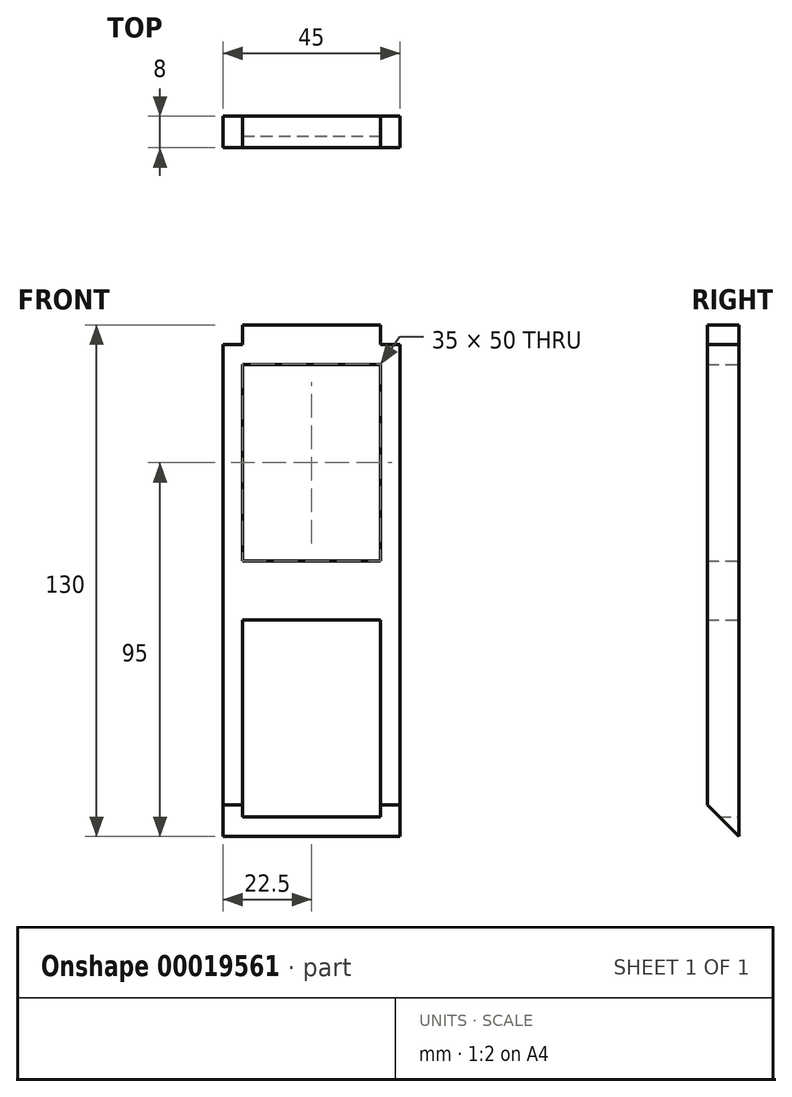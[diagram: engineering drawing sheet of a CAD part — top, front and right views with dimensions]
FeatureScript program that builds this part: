
annotation { "Feature Type Name" : "Feature", "Feature Type Description" : "" }
export const myFeature = defineFeature(function(context is Context, id is Id, definition is map)
    precondition{}
    {
        {
            var Q0;
            Q0=qCreatedBy(makeId("Front.planeOp"),FACE);
            var sketch = newSketch(context, id + "F0", { "sketchPlane" : qUnion([Q0])});
            skLineSegment(sketch, "E0.bottom", {"start": v(0, 0) * mm, "end": v(45, 0) * mm});
            skLineSegment(sketch, "E0.top", {"start": v(0, 125) * mm, "end": v(45, 125) * mm});
            skLineSegment(sketch, "E0.left", {"start": v(0, 0) * mm, "end": v(0, 125) * mm});
            skLineSegment(sketch, "E0.right", {"start": v(45, 0) * mm, "end": v(45, 125) * mm});
            skLineSegment(sketch, "E1.bottom", {"start": v(5, 120) * mm, "end": v(40, 120) * mm});
            skLineSegment(sketch, "E1.top", {"start": v(5, 70) * mm, "end": v(40, 70) * mm});
            skLineSegment(sketch, "E1.left", {"start": v(5, 120) * mm, "end": v(5, 70) * mm});
            skLineSegment(sketch, "E1.right", {"start": v(40, 120) * mm, "end": v(40, 70) * mm});
            skLineSegment(sketch, "E2.bottom", {"start": v(5, 55) * mm, "end": v(40, 55) * mm});
            skLineSegment(sketch, "E2.top", {"start": v(5, 5) * mm, "end": v(40, 5) * mm});
            skLineSegment(sketch, "E2.left", {"start": v(5, 55) * mm, "end": v(5, 5) * mm});
            skLineSegment(sketch, "E2.right", {"start": v(40, 55) * mm, "end": v(40, 5) * mm});
            skSolve(sketch);
        }
        {
            var Q0;
            Q0=makeQuery(id+"F0.imprint","IMPRINT",FACE,{"disambiguationData":[TD([[makeQuery(id+"F0.imprint","IMPRINT",EDGE,{"derivedFrom":sQuery(id+"F0.wireOp",EDGE,"E0.bottom")}),1.0]])]});
            extrude(context, id + "F1", {"entities" : qUnion([Q0]), "depth" : 8 * mm, "offsetDistance" : 25 * mm});
        }
        {
            var Q0;
            Q0=makeQuery(id+"F1.opExtrude","SWEPT_FACE",FACE,{"disambiguationData":[OSD([sQuery(id+"F0.wireOp",EDGE,"E0.top")])]});
            var sketch = newSketch(context, id + "F2", { "sketchPlane" : qUnion([Q0])});
            skLineSegment(sketch, "E3.bottom", {"start": v(5, 0) * mm, "end": v(40, 0) * mm});
            skLineSegment(sketch, "E3.top", {"start": v(5, -8) * mm, "end": v(40, -8) * mm});
            skLineSegment(sketch, "E3.left", {"start": v(5, 0) * mm, "end": v(5, -8) * mm});
            skLineSegment(sketch, "E3.right", {"start": v(40, 0) * mm, "end": v(40, -8) * mm});
            skSolve(sketch);
        }
        {
            var Q0;
            Q0 = qSketchRegion(id + "F2", true);
            extrude(context, id + "F3", {"entities" : qUnion([Q0]), "operationType" : NewBodyOperationType.ADD, "depth" : 5 * mm, "offsetDistance" : 25 * mm});
        }
        {
            var Q0;
            Q0=makeQuery(id+"F1.opExtrude","SWEPT_FACE",FACE,{"disambiguationData":[OSD([sQuery(id+"F0.wireOp",EDGE,"E0.left")])]});
            var sketch = newSketch(context, id + "F4", { "sketchPlane" : qUnion([Q0])});
            skLineSegment(sketch, "E4", {"start": v(0, 0) * mm, "end": v(8, 8) * mm});
            skLineSegment(sketch, "E5", {"start": v(8, 8) * mm, "end": v(8, 0) * mm});
            skLineSegment(sketch, "E6", {"start": v(8, 0) * mm, "end": v(0, 0) * mm});
            skSolve(sketch);
        }
        {
            var Q0;
            Q0 = qSketchRegion(id + "F4", true);
            extrude(context, id + "F5", {"entities" : qUnion([Q0]), "operationType" : NewBodyOperationType.REMOVE, "oppositeDirection" : true, "depth" : 60 * mm, "offsetDistance" : 25 * mm});
        }
    });
